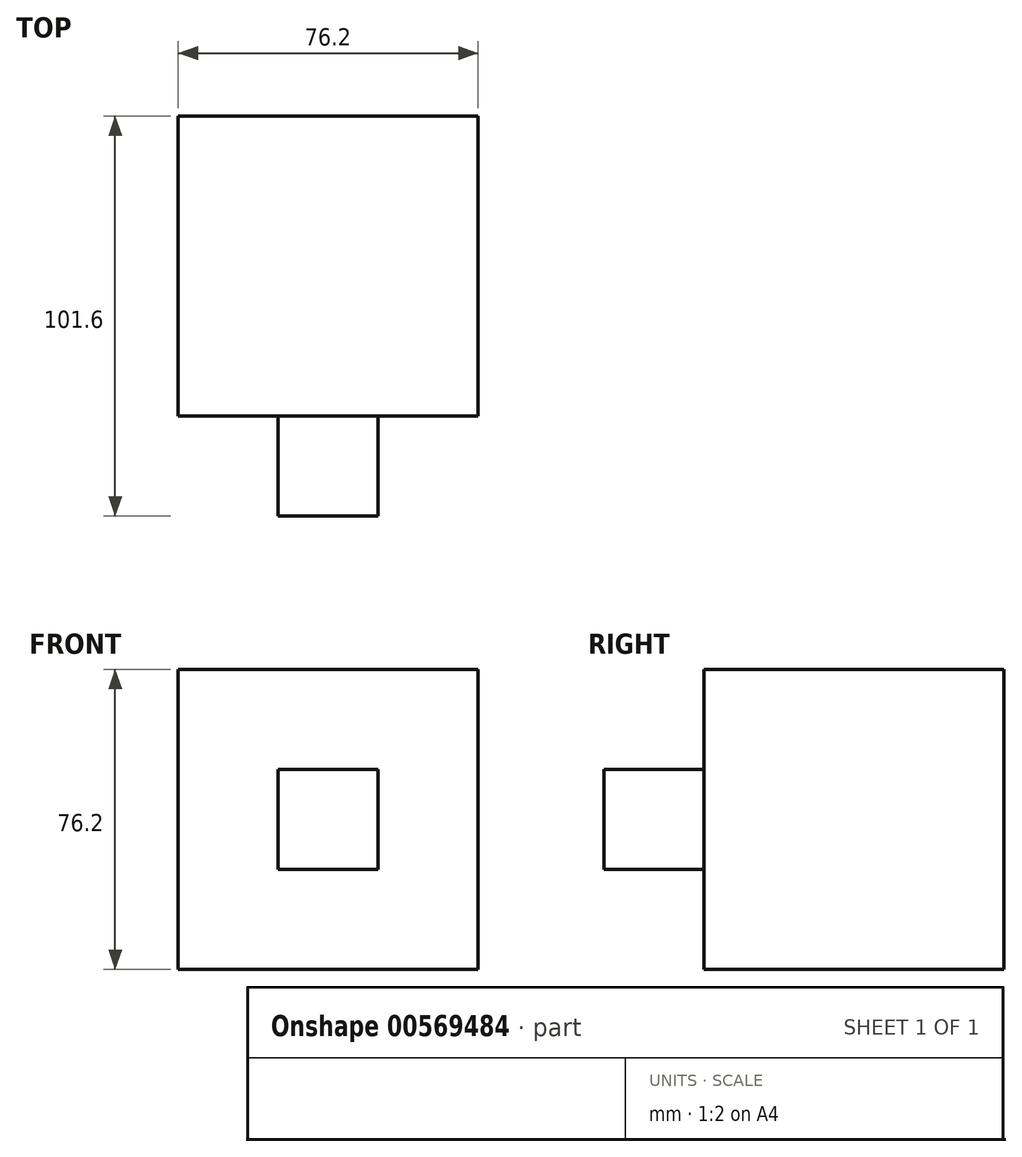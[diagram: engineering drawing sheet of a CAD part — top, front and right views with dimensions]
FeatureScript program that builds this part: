
annotation { "Feature Type Name" : "Feature", "Feature Type Description" : "" }
export const myFeature = defineFeature(function(context is Context, id is Id, definition is map)
    precondition{}
    {
        {
            var Q0;
            Q0=qCreatedBy(makeId("Front.planeOp"),FACE);
            var sketch = newSketch(context, id + "F0", { "sketchPlane" : qUnion([Q0])});
            skLineSegment(sketch, "E0.bottom", {"start": v(-76.2, 86.96) * mm, "end": v(0, 86.96) * mm});
            skLineSegment(sketch, "E0.top", {"start": v(-76.2, 10.76) * mm, "end": v(0, 10.76) * mm});
            skLineSegment(sketch, "E0.left", {"start": v(-76.2, 86.96) * mm, "end": v(-76.2, 10.76) * mm});
            skLineSegment(sketch, "E0.right", {"start": v(0, 86.96) * mm, "end": v(0, 10.76) * mm});
            skSolve(sketch);
        }
        {
            var Q0;
            Q0=makeQuery(id+"F0.imprint","IMPRINT",FACE,{"disambiguationData":[TD([[makeQuery(id+"F0.imprint","IMPRINT",EDGE,{"derivedFrom":sQuery(id+"F0.wireOp",EDGE,"E0.bottom")}),-1.0]])]});
            extrude(context, id + "F1", {"entities" : qUnion([Q0]), "depth" : 76.2 * mm, "offsetDistance" : 25.4 * mm});
        }
        {
            var Q0;
            Q0=makeQuery(id+"F1.opExtrude","CAP_FACE",FACE,{"disambiguationData":[OSD([sQuery(id+"F0.wireOp",EDGE,"E0.bottom"),sQuery(id+"F0.wireOp",EDGE,"E0.top"),sQuery(id+"F0.wireOp",EDGE,"E0.left"),sQuery(id+"F0.wireOp",EDGE,"E0.right")])],"isStart":false});
            var sketch = newSketch(context, id + "F2", { "sketchPlane" : qUnion([Q0])});
            skLineSegment(sketch, "E1.bottom", {"start": v(-50.8, 61.56) * mm, "end": v(-25.4, 61.56) * mm});
            skLineSegment(sketch, "E1.top", {"start": v(-50.8, 36.16) * mm, "end": v(-25.4, 36.16) * mm});
            skLineSegment(sketch, "E1.left", {"start": v(-50.8, 61.56) * mm, "end": v(-50.8, 36.16) * mm});
            skLineSegment(sketch, "E1.right", {"start": v(-25.4, 61.56) * mm, "end": v(-25.4, 36.16) * mm});
            skSolve(sketch);
        }
        {
            var Q0;
            Q0=makeQuery(id+"F2.imprint","IMPRINT",FACE,{"disambiguationData":[TD([[makeQuery(id+"F2.imprint","IMPRINT",EDGE,{"derivedFrom":sQuery(id+"F2.wireOp",EDGE,"E1.bottom")}),-1.0]])]});
            extrude(context, id + "F3", {"entities" : qUnion([Q0]), "operationType" : NewBodyOperationType.ADD, "depth" : 25.4 * mm, "offsetDistance" : 25.4 * mm});
        }
    });
